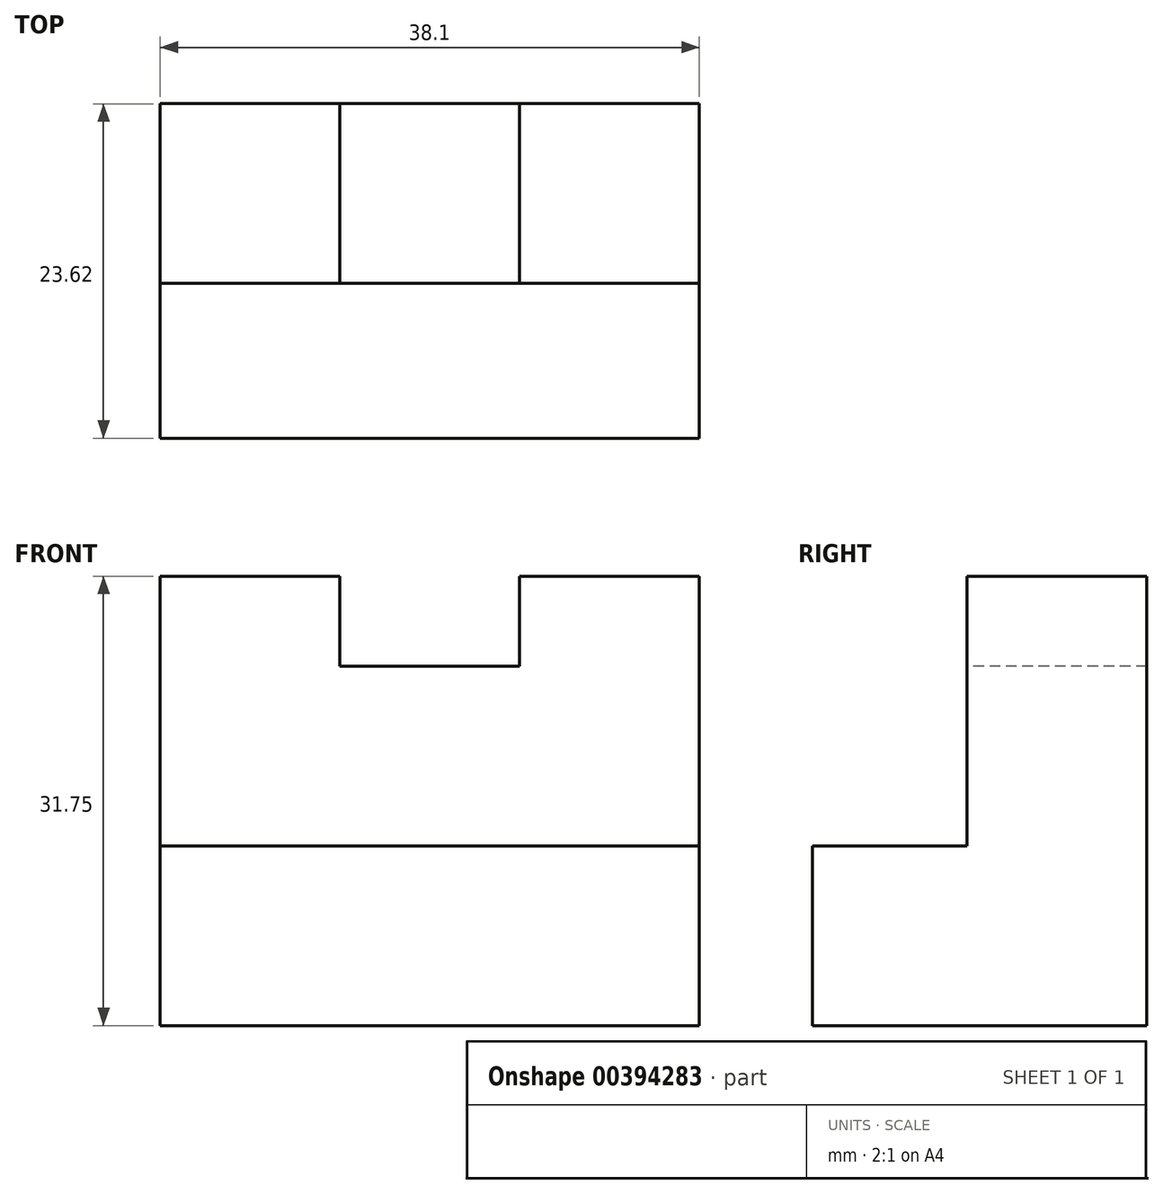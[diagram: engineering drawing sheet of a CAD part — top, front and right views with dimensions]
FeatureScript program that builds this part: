
annotation { "Feature Type Name" : "Feature", "Feature Type Description" : "" }
export const myFeature = defineFeature(function(context is Context, id is Id, definition is map)
    precondition{}
    {
        {
            var Q0;
            Q0=qCreatedBy(makeId("Right.planeOp"),FACE);
            var sketch = newSketch(context, id + "F0", { "sketchPlane" : qUnion([Q0])});
            skLineSegment(sketch, "E0", {"start": v(0, 0) * mm, "end": v(0, 12.7) * mm});
            skLineSegment(sketch, "E1", {"start": v(10.92, 12.7) * mm, "end": v(0, 12.7) * mm});
            skLineSegment(sketch, "E2", {"start": v(10.92, 12.7) * mm, "end": v(10.92, 31.75) * mm});
            skLineSegment(sketch, "E3", {"start": v(10.92, 31.75) * mm, "end": v(23.62, 31.75) * mm});
            skLineSegment(sketch, "E4", {"start": v(23.62, 31.75) * mm, "end": v(23.62, 0) * mm});
            skLineSegment(sketch, "E5", {"start": v(23.62, 0) * mm, "end": v(0, 0) * mm});
            skSolve(sketch);
        }
        {
            var Q0;
            Q0 = qSketchRegion(id + "F0", true);
            extrude(context, id + "F1", {"entities" : qUnion([Q0]), "depth" : 38.1 * mm});
        }
        {
            var Q0;
            Q0=makeQuery(id+"F1.opExtrude","SWEPT_FACE",FACE,{"disambiguationData":[OSD([sQuery(id+"F0.wireOp",EDGE,"E2")])]});
            var sketch = newSketch(context, id + "F2", { "sketchPlane" : qUnion([Q0])});
            skLineSegment(sketch, "E6", {"start": v(0, 31.75) * mm, "end": v(12.7, 31.75) * mm});
            skLineSegment(sketch, "E7", {"start": v(12.7, 31.75) * mm, "end": v(12.7, 25.4) * mm});
            skLineSegment(sketch, "E8", {"start": v(12.7, 25.4) * mm, "end": v(25.4, 25.4) * mm});
            skLineSegment(sketch, "E9", {"start": v(25.4, 25.4) * mm, "end": v(25.4, 31.75) * mm});
            skSolve(sketch);
        }
        {
            var Q0;
            Q0 = qSketchRegion(id + "F2", true);
            var Q1;
            {var subQ0=sQuery(id+"F2.wireOp",EDGE,"E7");Q1=makeQuery(id+"F2.imprint","IMPRINT",FACE,{"disambiguationData":[TD([[makeQuery(id+"F2.imprint","IMPRINT",EDGE,{"derivedFrom":subQ0}),1.0]])]});}
            extrude(context, id + "F3", {"entities" : qUnion([Q0, Q1]), "operationType" : NewBodyOperationType.REMOVE, "oppositeDirection" : true, "depth" : 25.4 * mm});
        }
    });
